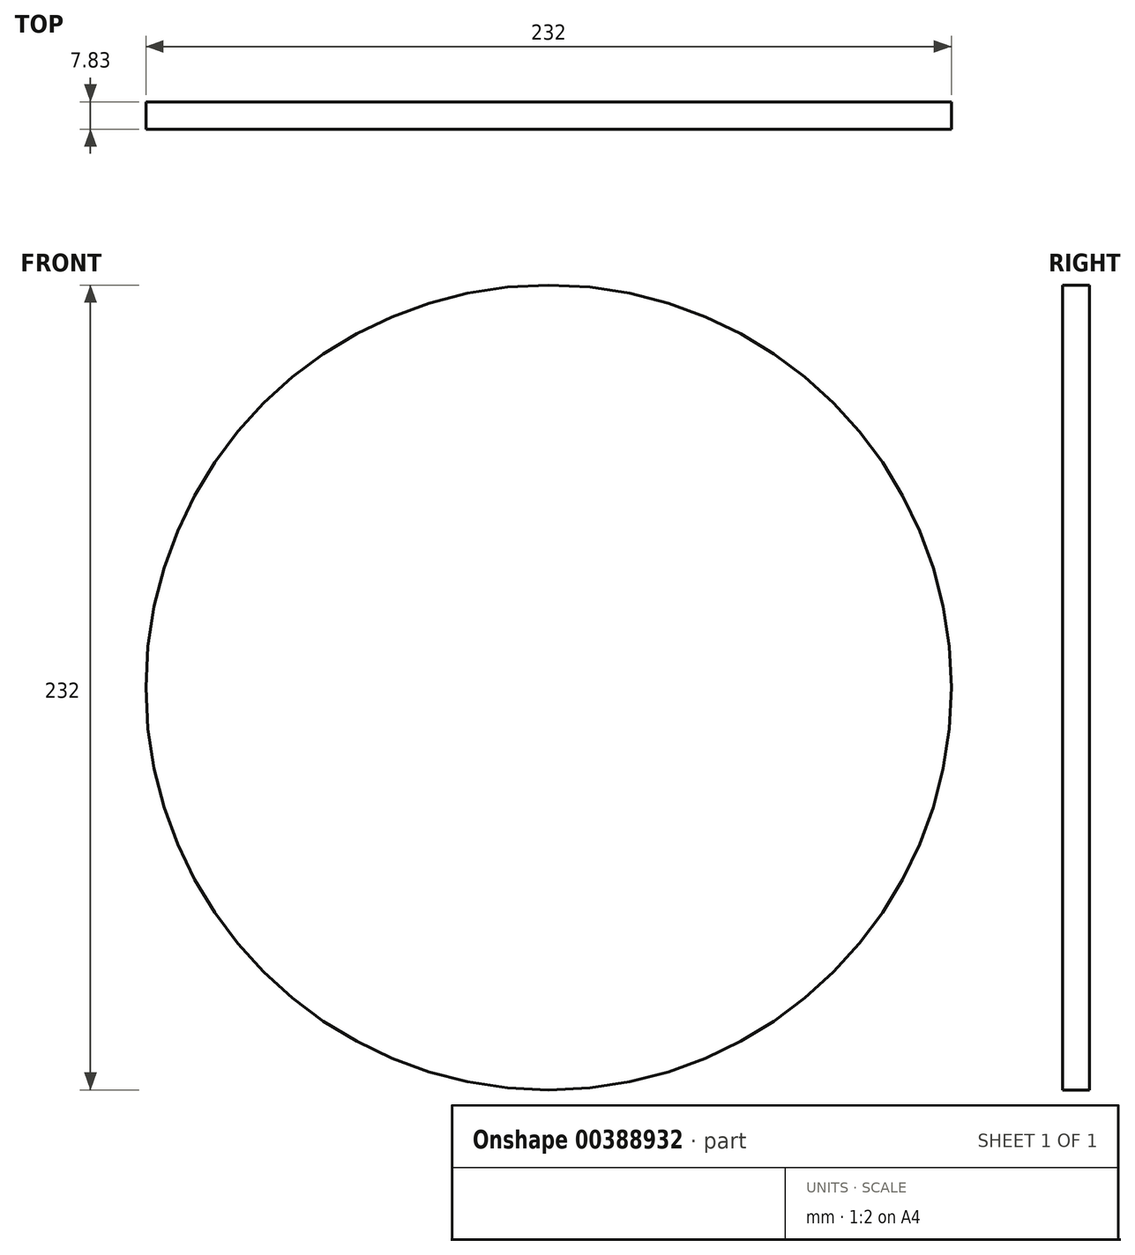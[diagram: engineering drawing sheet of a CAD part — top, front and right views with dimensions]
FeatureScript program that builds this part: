
annotation { "Feature Type Name" : "Feature", "Feature Type Description" : "" }
export const myFeature = defineFeature(function(context is Context, id is Id, definition is map)
    precondition{}
    {
        {
            var Q0;
            Q0=qCreatedBy(makeId("Front.planeOp"),FACE);
            var sketch = newSketch(context, id + "F0", { "sketchPlane" : qUnion([Q0])});
            skCircle(sketch, "E0", {"center": v(0, 0) * mm, "radius": 44.45 * mm});
            skSolve(sketch);
        }
        {
            var Q0;
            Q0 = qSketchRegion(id + "F0", true);
            extrude(context, id + "F1", {"entities" : qUnion([Q0]), "depth" : 3 * mm});
        }
        {
            var Q0;
            Q0=makeQuery(id+"F1.opExtrude","SWEPT_BODY",BODY,{"disambiguationData":[OSD([sQuery(id+"F0.wireOp",EDGE,"E0")])]});
            var Q1;
            Q1=qCreatedBy(makeId("Origin.pointOp"),VERTEX);
            transform(context, id + "F2", {"entities" : qUnion([Q0]), "transformType" : TransformType.SCALE_UNIFORMLY, "scale" : 2.6, "scalePoint" : qUnion([Q1]), "makeCopy" : false});
        }
    });
